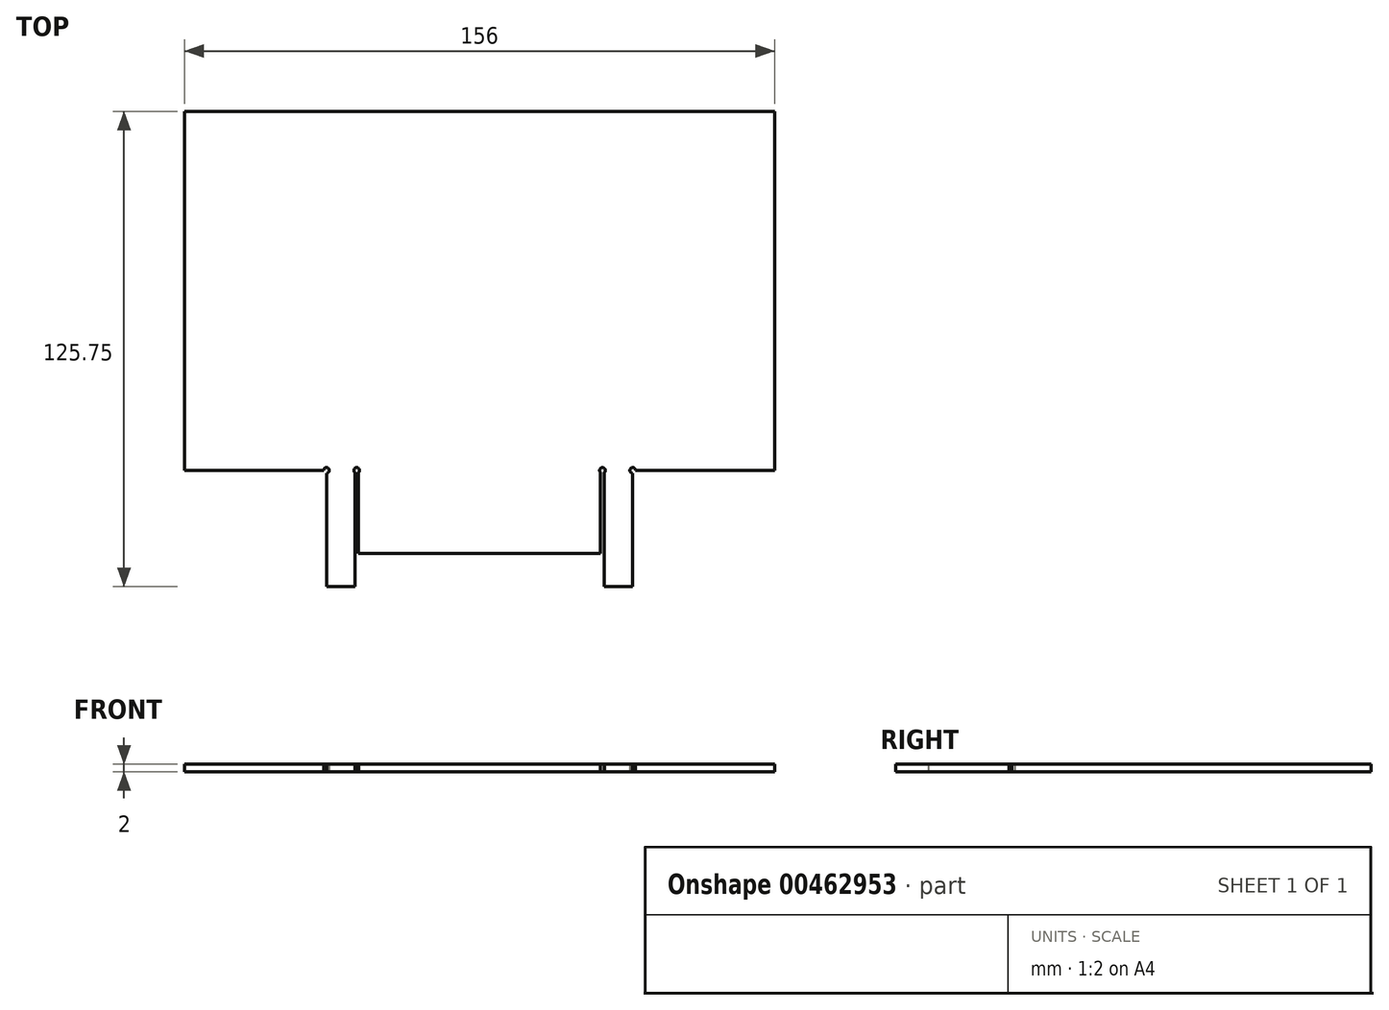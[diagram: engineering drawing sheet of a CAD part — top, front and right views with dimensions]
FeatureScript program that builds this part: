
annotation { "Feature Type Name" : "Feature", "Feature Type Description" : "" }
export const myFeature = defineFeature(function(context is Context, id is Id, definition is map)
    precondition{}
    {
        {
            var Q0;
            Q0=qCreatedBy(makeId("Top.planeOp"),FACE);
            var sketch = newSketch(context, id + "F0", { "sketchPlane" : qUnion([Q0])});
            skLineSegment(sketch, "E0", {"start": v(0, 117) * mm, "end": v(-78, 117) * mm});
            skLineSegment(sketch, "E1", {"start": v(-78, 117) * mm, "end": v(-78, 22) * mm});
            skLineSegment(sketch, "E2", {"start": v(-78, 22) * mm, "end": v(-41.25, 22) * mm});
            skLineSegment(sketch, "E3", {"start": v(-40.5, 21.25) * mm, "end": v(-40.5, -8.75) * mm});
            skLineSegment(sketch, "E4", {"start": v(0, 0) * mm, "end": v(-32, 0) * mm});
            skLineSegment(sketch, "E5", {"start": v(-32, 0) * mm, "end": v(-32, 21.44) * mm});
            skLineSegment(sketch, "E6", {"start": v(-33, 21.44) * mm, "end": v(-33, -8.75) * mm});
            skLineSegment(sketch, "E7", {"start": v(-33, -8.75) * mm, "end": v(-40.5, -8.75) * mm});
            skLineSegment(sketch, "E8.MirrorCS", {"start": v(78, 117) * mm, "end": v(78, 22) * mm});
            skLineSegment(sketch, "E9.MirrorCS", {"start": v(0, 117) * mm, "end": v(78, 117) * mm});
            skLineSegment(sketch, "E10.MirrorCS", {"start": v(0, 0) * mm, "end": v(32, 0) * mm});
            skLineSegment(sketch, "E11.MirrorCS", {"start": v(78, 22) * mm, "end": v(40.5, 22) * mm});
            skArc(sketch, "E12", {"start": v(-40.5, 21.25) * mm, "mid": v(-39.97, 22.53) * mm, "end": v(-41.25, 22) * mm});
            skPoint(sketch, "E13.orphan", {"position": v(-32, 22) * mm});
            skPoint(sketch, "E14.end.orphan", {"position": v(-33, 22) * mm});
            skLineSegment(sketch, "E15", {"start": v(-33, 22) * mm, "end": v(-32, 22) * mm, "construction": true});
            skPoint(sketch, "E16", {"position": v(-32.5, 22) * mm});
            skArc(sketch, "E17", {"start": v(-32, 21.44) * mm, "mid": v(-32.5, 22.75) * mm, "end": v(-33, 21.44) * mm});
            skLineSegment(sketch, "E18.MirrorCS", {"start": v(33, 22) * mm, "end": v(32, 22) * mm, "construction": true});
            skArc(sketch, "E19.MirrorCS", {"start": v(32, 21.44) * mm, "mid": v(32.5, 22.75) * mm, "end": v(33, 21.44) * mm});
            skArc(sketch, "E20.MirrorCS", {"start": v(40.5, 21.25) * mm, "mid": v(39.97, 22.53) * mm, "end": v(41.25, 22) * mm});
            skLineSegment(sketch, "E21.MirrorCS", {"start": v(40.5, 21.25) * mm, "end": v(40.5, -8.75) * mm});
            skPoint(sketch, "E22.MirrorP", {"position": v(32, 22) * mm});
            skLineSegment(sketch, "E23.MirrorCS", {"start": v(33, -8.75) * mm, "end": v(40.5, -8.75) * mm});
            skPoint(sketch, "E24.MirrorP", {"position": v(33, 22) * mm});
            skLineSegment(sketch, "E25.MirrorCS", {"start": v(33, 21.44) * mm, "end": v(33, -8.75) * mm});
            skLineSegment(sketch, "E26.MirrorCS", {"start": v(32, 0) * mm, "end": v(32, 21.44) * mm});
            skSolve(sketch);
        }
        {
            var Q0;
            Q0=makeQuery(id+"F0.imprint","IMPRINT",FACE,{"disambiguationData":[TD([[makeQuery(id+"F0.imprint","IMPRINT",EDGE,{"derivedFrom":sQuery(id+"F0.wireOp",EDGE,"E0")}),1.0]])]});
            extrude(context, id + "F1", {"entities" : qUnion([Q0]), "depth" : 2 * mm, "offsetDistance" : 25 * mm});
        }
    });
